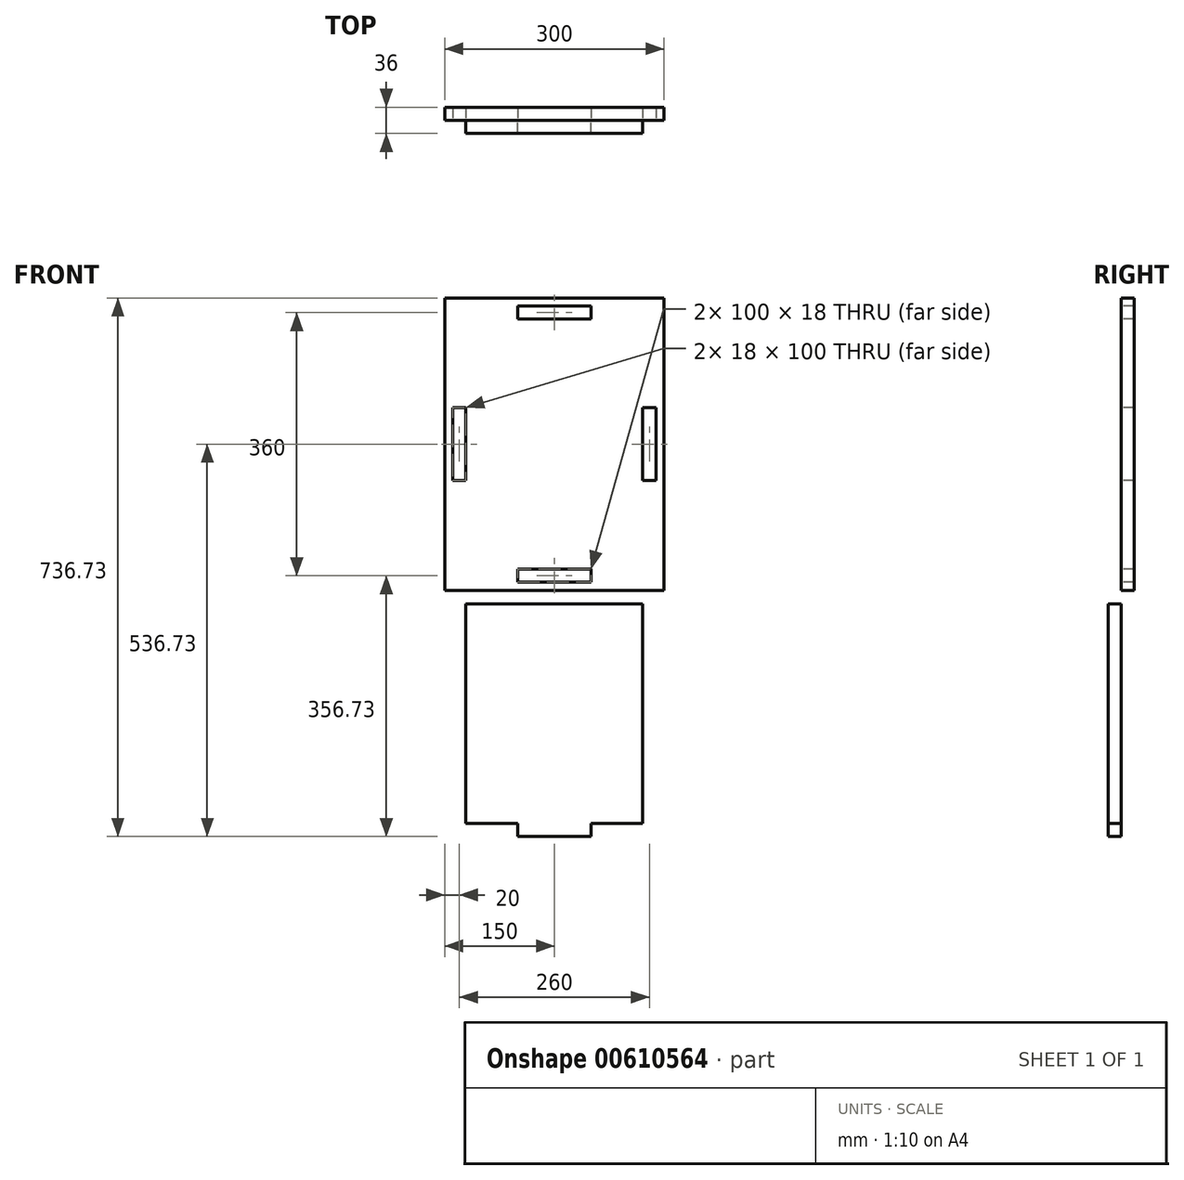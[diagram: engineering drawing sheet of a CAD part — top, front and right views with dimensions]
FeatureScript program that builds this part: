
annotation { "Feature Type Name" : "Feature", "Feature Type Description" : "" }
export const myFeature = defineFeature(function(context is Context, id is Id, definition is map)
    precondition{}
    {
        {
            var Q0;
            Q0=qCreatedBy(makeId("Front.planeOp"),FACE);
            var sketch = newSketch(context, id + "F0", { "sketchPlane" : qUnion([Q0])});
            skLineSegment(sketch, "E0.bottom", {"start": v(-150, 200) * mm, "end": v(150, 200) * mm});
            skLineSegment(sketch, "E0.top", {"start": v(-150, -200) * mm, "end": v(150, -200) * mm});
            skLineSegment(sketch, "E0.left", {"start": v(-150, 200) * mm, "end": v(-150, -200) * mm});
            skLineSegment(sketch, "E0.right", {"start": v(150, 200) * mm, "end": v(150, -200) * mm});
            skPoint(sketch, "E0.middle", {"position": v(0, 0) * mm});
            skSolve(sketch);
        }
        {
            var Q0;
            Q0=makeQuery(id+"F0.imprint","IMPRINT",FACE,{"disambiguationData":[TD([[makeQuery(id+"F0.imprint","IMPRINT",EDGE,{"derivedFrom":sQuery(id+"F0.wireOp",EDGE,"E0.bottom")}),-1.0]])]});
            extrude(context, id + "F1", {"entities" : qUnion([Q0]), "depth" : 18 * mm, "offsetDistance" : 25 * mm});
        }
        {
            var Q0;
            Q0=makeQuery(id+"F1.opExtrude","CAP_FACE",FACE,{"disambiguationData":[OSD([sQuery(id+"F0.wireOp",EDGE,"E0.bottom"),sQuery(id+"F0.wireOp",EDGE,"E0.top"),sQuery(id+"F0.wireOp",EDGE,"E0.left"),sQuery(id+"F0.wireOp",EDGE,"E0.right")])],"isStart":false});
            var sketch = newSketch(context, id + "F2", { "sketchPlane" : qUnion([Q0])});
            skLineSegment(sketch, "E1.bottom", {"start": v(50, -180) * mm, "end": v(-50, -180) * mm});
            skLineSegment(sketch, "E1.top", {"start": v(50, 180) * mm, "end": v(-50, 180) * mm});
            skLineSegment(sketch, "E1.left", {"start": v(130, -50) * mm, "end": v(130, 50) * mm});
            skLineSegment(sketch, "E1.right", {"start": v(-130, -50) * mm, "end": v(-130, 50) * mm});
            skPoint(sketch, "E1.middle", {"position": v(0, 0) * mm});
            skLineSegment(sketch, "E2.bottom", {"start": v(-121, -50) * mm, "end": v(-139, -50) * mm});
            skLineSegment(sketch, "E2.top", {"start": v(-121, 50) * mm, "end": v(-139, 50) * mm});
            skLineSegment(sketch, "E2.left", {"start": v(-121, -50) * mm, "end": v(-121, 50) * mm});
            skLineSegment(sketch, "E2.right", {"start": v(-139, -50) * mm, "end": v(-139, 50) * mm});
            skPoint(sketch, "E2.middle", {"position": v(-130, 0) * mm});
            skLineSegment(sketch, "E3.bottom", {"start": v(121, 50) * mm, "end": v(139, 50) * mm});
            skLineSegment(sketch, "E3.top", {"start": v(121, -50) * mm, "end": v(139, -50) * mm});
            skLineSegment(sketch, "E3.left", {"start": v(121, 50) * mm, "end": v(121, -50) * mm});
            skLineSegment(sketch, "E3.right", {"start": v(139, 50) * mm, "end": v(139, -50) * mm});
            skPoint(sketch, "E3.middle", {"position": v(130, 0) * mm});
            skLineSegment(sketch, "E4.bottom", {"start": v(50, 171) * mm, "end": v(-50, 171) * mm});
            skLineSegment(sketch, "E4.top", {"start": v(50, 189) * mm, "end": v(-50, 189) * mm});
            skLineSegment(sketch, "E4.left", {"start": v(50, 171) * mm, "end": v(50, 189) * mm});
            skLineSegment(sketch, "E4.right", {"start": v(-50, 171) * mm, "end": v(-50, 189) * mm});
            skPoint(sketch, "E4.middle", {"position": v(0, 180) * mm});
            skLineSegment(sketch, "E5.bottom", {"start": v(-50, -171) * mm, "end": v(50, -171) * mm});
            skLineSegment(sketch, "E5.top", {"start": v(-50, -189) * mm, "end": v(50, -189) * mm});
            skLineSegment(sketch, "E5.left", {"start": v(-50, -171) * mm, "end": v(-50, -189) * mm});
            skLineSegment(sketch, "E5.right", {"start": v(50, -171) * mm, "end": v(50, -189) * mm});
            skPoint(sketch, "E5.middle", {"position": v(0, -180) * mm});
            skPoint(sketch, "E6.orphan", {"position": v(130, 180) * mm});
            skPoint(sketch, "E7.orphan", {"position": v(-130, 180) * mm});
            skPoint(sketch, "E8.orphan", {"position": v(-130, -180) * mm});
            skPoint(sketch, "E9.orphan", {"position": v(130, -180) * mm});
            skSolve(sketch);
        }
        {
            var Q0;
            Q0 = qSketchRegion(id + "F2", true);
            extrude(context, id + "F3", {"entities" : qUnion([Q0]), "operationType" : NewBodyOperationType.REMOVE, "oppositeDirection" : true, "depth" : 25 * mm, "offsetDistance" : 25 * mm});
        }
        {
            var Q0;
            Q0=makeQuery(id+"F1.opExtrude","CAP_FACE",FACE,{"disambiguationData":[OSD([sQuery(id+"F0.wireOp",EDGE,"E0.bottom"),sQuery(id+"F0.wireOp",EDGE,"E0.top"),sQuery(id+"F0.wireOp",EDGE,"E0.left"),sQuery(id+"F0.wireOp",EDGE,"E0.right")])],"isStart":false});
            var sketch = newSketch(context, id + "F4", { "sketchPlane" : qUnion([Q0])});
            skLineSegment(sketch, "E10.bottom", {"start": v(-121, -218.73) * mm, "end": v(121, -218.73) * mm});
            skLineSegment(sketch, "E10.top", {"start": v(-121, -518.73) * mm, "end": v(-50, -518.73) * mm});
            skLineSegment(sketch, "E10.left", {"start": v(-121, -218.73) * mm, "end": v(-121, -518.73) * mm});
            skLineSegment(sketch, "E10.right", {"start": v(121, -218.73) * mm, "end": v(121, -518.73) * mm});
            skLineSegment(sketch, "E11.bottom", {"start": v(50, -536.73) * mm, "end": v(-50, -536.73) * mm});
            skLineSegment(sketch, "E11.left", {"start": v(50, -536.73) * mm, "end": v(50, -518.73) * mm});
            skLineSegment(sketch, "E11.right", {"start": v(-50, -536.73) * mm, "end": v(-50, -518.73) * mm});
            skPoint(sketch, "E11.middle", {"position": v(0, -518.73) * mm});
            skPoint(sketch, "E12.orphan", {"position": v(50, -500.73) * mm});
            skPoint(sketch, "E13.orphan", {"position": v(-50, -500.73) * mm});
            skLineSegment(sketch, "E14.trimOffspring", {"start": v(50, -518.73) * mm, "end": v(121, -518.73) * mm});
            skSolve(sketch);
        }
        {
            var Q0;
            Q0 = qSketchRegion(id + "F4", true);
            extrude(context, id + "F5", {"entities" : qUnion([Q0]), "depth" : 18 * mm, "offsetDistance" : 25 * mm});
        }
    });
